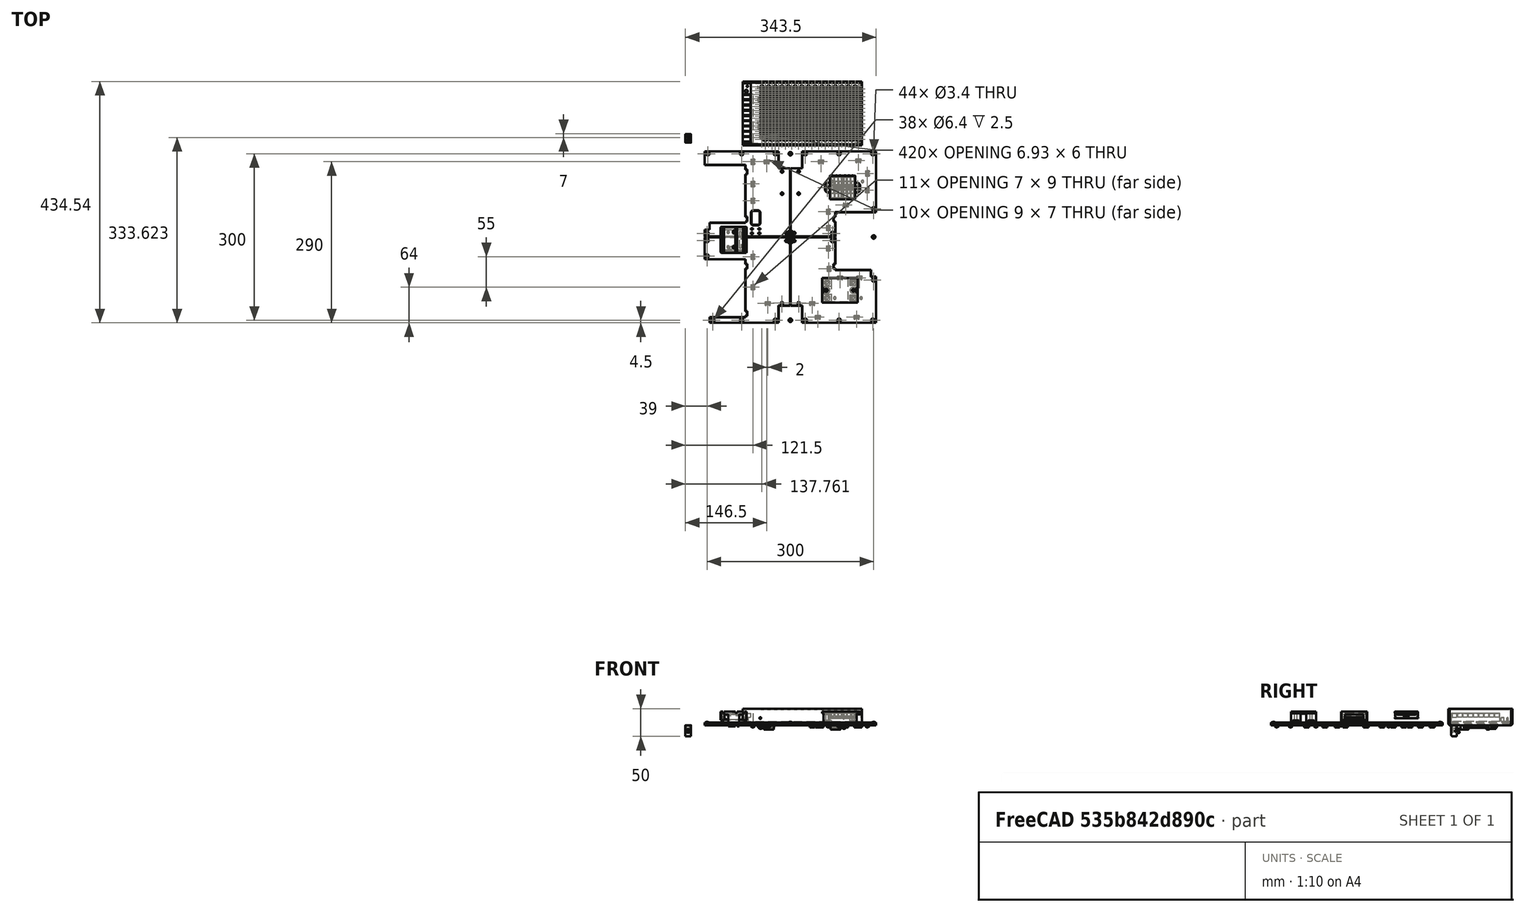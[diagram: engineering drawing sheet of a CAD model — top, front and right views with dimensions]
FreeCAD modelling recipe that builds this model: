
FCSTD DOCUMENT  (FreeCAD 0.19R24291 (Git))
Label: bottom-plate-180
License: All rights reserved
LicenseURL: http://en.wikipedia.org/wiki/All_rights_reserved
objects: Part::Feature×67, Part::MultiFuse×18, Part::Cylinder×16, Part::Box×9, Part::Cut×9, Part::FeaturePython×6, Part::Chamfer×5, App::Part×4, Part::MultiCommon×4
note: 134 computed .brp shape members not serialized (recipe doc carries the construction recipe); baked Part::Feature solids carry a one-line shape summary decoded from their .brp

FEATURE [Part::Feature] Cut001003002001  label="motor-cut-slot"
  Placement = pos=(-155,-155,0) rot=(0,0,1;0rad)
  shape: bbox 77 x 116.1 x 10 mm, 16 faces (baked)
FEATURE [Part::Box] Box  label="Cube"
  AttacherType = Attacher::AttachEngine3D
  Height = 5
  Length = 309
  Placement = pos=(-154.5,-154.5,0) rot=(0,0,1;0rad)
  Width = 309
FEATURE [Part::Feature] Cut001003002002  label="motor-cut-slot001"
  Placement = pos=(-155,15,0) rot=(0,0,1;0rad)
  shape: bbox 77 x 116.1 x 10 mm, 16 faces (baked)
FEATURE [Part::Feature] Part__Mirroring001  label="motor-cut-slot (Mirror #1)001"
  Placement = pos=(0,85,0) rot=(0,0,1;0rad)
  shape: bbox 77 x 116.1 x 10 mm, 16 faces (baked)
FEATURE [Part::MultiFuse] Fusion
  Shapes = -> [Part__Mirroring001,Cut001003002002,Cut001003002001]
FEATURE [Part::Cut] Cut
  Base = -> Box
  Tool = -> Fusion
FEATURE [Part::Box] Box002  label="Cube002"
  AttacherType = Attacher::AttachEngine3D
  Height = 10
  Length = 42
  Placement = pos=(-21,-155,0) rot=(0,0,1;0rad)
  Width = 31
FEATURE [Part::Box] Box003  label="Cube003"
  AttacherType = Attacher::AttachEngine3D
  Height = 10
  Length = 42
  Placement = pos=(-21,124,0) rot=(0,0,1;0rad)
  Width = 31
FEATURE [Part::MultiFuse] Fusion001
  Shapes = -> [Box003,Box002]
FEATURE [Part::Cut] Cut001003002003
  Base = -> Cut
  Tool = -> Fusion001
FEATURE [Part::Cylinder] Cylinder
  Angle = 360
  AttacherType = Attacher::AttachEngine3D
  Height = 10
  Placement = pos=(-15,-119,0) rot=(0,0,1;0rad)
  Radius = 1.7
FEATURE [Part::Cylinder] Cylinder001
  Angle = 360
  AttacherType = Attacher::AttachEngine3D
  Height = 10
  Placement = pos=(15,-119,0) rot=(0,0,1;0rad)
  Radius = 1.7
FEATURE [Part::Cylinder] Cylinder002
  Angle = 360
  AttacherType = Attacher::AttachEngine3D
  Height = 10
  Placement = pos=(-7,7,0) rot=(0,0,1;0rad)
  Radius = 1.9
FEATURE [Part::Cylinder] Cylinder003
  Angle = 360
  AttacherType = Attacher::AttachEngine3D
  Height = 10
  Placement = pos=(7,7,0) rot=(0,0,1;0rad)
  Radius = 1.9
FEATURE [Part::Cylinder] Cylinder004
  Angle = 360
  AttacherType = Attacher::AttachEngine3D
  Height = 10
  Placement = pos=(-7,-7,0) rot=(0,0,1;0rad)
  Radius = 1.9
FEATURE [Part::Cylinder] Cylinder005
  Angle = 360
  AttacherType = Attacher::AttachEngine3D
  Height = 10
  Placement = pos=(7,-7,0) rot=(0,0,1;0rad)
  Radius = 1.9
FEATURE [Part::MultiFuse] Fusion003
  Shapes = -> [Cylinder005,Cylinder002,Cylinder003,Cylinder004]
FEATURE [Part::Box] Box004  label="Cube004"
  AttacherType = Attacher::AttachEngine3D
  Height = 10
  Length = 310
  Placement = pos=(-155,-0.5,0) rot=(0,0,1;0rad)
  Width = 1
FEATURE [Part::Box] Box005  label="Cube005"
  AttacherType = Attacher::AttachEngine3D
  Height = 10
  Length = 1
  Placement = pos=(-0.5,-155,0) rot=(0,0,1;0rad)
  Width = 310
FEATURE [Part::MultiFuse] Fusion004  label="separatpr"
  Shapes = -> [Box005,Box004]
FEATURE [Part::Feature] Fusion005030001  label="bed-cable"
  Placement = pos=(35,-24,0) rot=(0,0,1;0rad)
  shape: bbox 15 x 42 x 10 mm, 34 faces, 5 solids (baked)
FEATURE [Part::Cylinder] Cylinder008
  Angle = 360
  AttacherType = Attacher::AttachEngine3D
  Height = 10
  Placement = pos=(-15,118,0) rot=(0,0,1;0rad)
  Radius = 1.9
FEATURE [Part::Cylinder] Cylinder009
  Angle = 360
  AttacherType = Attacher::AttachEngine3D
  Height = 10
  Placement = pos=(15,118,0) rot=(0,0,1;0rad)
  Radius = 1.9
FEATURE [Part::Cylinder] Cylinder010
  Angle = 360
  AttacherType = Attacher::AttachEngine3D
  Height = 10
  Placement = pos=(15,78,0) rot=(0,0,1;0rad)
  Radius = 1.9
FEATURE [Part::Cylinder] Cylinder011
  Angle = 360
  AttacherType = Attacher::AttachEngine3D
  Height = 10
  Placement = pos=(-15,78,0) rot=(0,0,1;0rad)
  Radius = 1.9
FEATURE [Part::MultiFuse] Fusion005030003
  Shapes = -> [Cylinder011,Cylinder008,Cylinder009,Cylinder010]
FEATURE [Part::Feature] Fusion005030004  label="bolt-slot"
  shape: bbox 6.4 x 6.4 x 6 mm, 7 faces (baked)
FEATURE [Part::Feature] Fusion005030005  label="bolt-slot_U"
  Placement = pos=(0,150,0) rot=(0,0,1;0rad)
  shape: bbox 6.4 x 6.4 x 6 mm, 7 faces (baked)
FEATURE [Part::Feature] Fusion005030006  label="bolt-slot_D"
  Placement = pos=(0,-150,0) rot=(0,0,1;0rad)
  shape: bbox 6.4 x 6.4 x 6 mm, 7 faces (baked)
FEATURE [Part::Feature] Fusion005030007  label="bolt-slot_L"
  Placement = pos=(-150,0,0) rot=(0,0,1;0rad)
  shape: bbox 6.4 x 6.4 x 6 mm, 7 faces (baked)
FEATURE [Part::Feature] Fusion005030008  label="bolt-slot_R"
  Placement = pos=(150,0,0) rot=(0,0,1;0rad)
  shape: bbox 6.4 x 6.4 x 6 mm, 7 faces (baked)
FEATURE [Part::Feature] Fusion005030009  label="bolt-slot_U001"
  Placement = pos=(-27,150,0) rot=(0,0,1;0rad)
  shape: bbox 6.4 x 6.4 x 6 mm, 7 faces (baked)
FEATURE [Part::Feature] Fusion005030010  label="bolt-slot_U002"
  Placement = pos=(27,150,0) rot=(0,0,1;0rad)
  shape: bbox 6.4 x 6.4 x 6 mm, 7 faces (baked)
FEATURE [Part::Feature] Fusion005030011  label="bolt-slot_U003"
  Placement = pos=(-148.5,150,0) rot=(0,0,1;0rad)
  shape: bbox 6.4 x 6.4 x 6 mm, 7 faces (baked)
FEATURE [Part::Feature] Fusion005030012  label="bolt-slot_U004"
  Placement = pos=(148.5,150,0) rot=(0,0,1;0rad)
  shape: bbox 6.4 x 6.4 x 6 mm, 7 faces (baked)
FEATURE [Part::Feature] Fusion005030013  label="bolt-slot_U005"
  Placement = pos=(-87.75,150,0) rot=(0,0,1;0rad)
  shape: bbox 6.4 x 6.4 x 6 mm, 7 faces (baked)
FEATURE [Part::Feature] Fusion005030014  label="bolt-slot_U006"
  Placement = pos=(87.75,150,0) rot=(0,0,1;0rad)
  shape: bbox 6.4 x 6.4 x 6 mm, 7 faces (baked)
FEATURE [Part::MultiFuse] Fusion005030015
  Shapes = -> [Fusion005030009,Fusion005030010,Fusion005030011,Fusion005030012,Fusion005030013,Fusion005030014]
FEATURE [Part::Feature] Fusion005030016  label="bolt-slot_D001"
  Placement = pos=(27,-150,0) rot=(0,0,1;0rad)
  shape: bbox 6.4 x 6.4 x 6 mm, 7 faces (baked)
FEATURE [Part::Feature] Fusion005030017  label="bolt-slot_D002"
  Placement = pos=(-27,-150,0) rot=(0,0,1;0rad)
  shape: bbox 6.4 x 6.4 x 6 mm, 7 faces (baked)
FEATURE [Part::Feature] Fusion005030018  label="bolt-slot_D003"
  Placement = pos=(148.5,-150,0) rot=(0,0,1;0rad)
  shape: bbox 6.4 x 6.4 x 6 mm, 7 faces (baked)
FEATURE [Part::Feature] Fusion005030019  label="bolt-slot_D004"
  Placement = pos=(-139.5,-150,0) rot=(0,0,1;0rad)
  shape: bbox 6.4 x 6.4 x 6 mm, 7 faces (baked)
FEATURE [Part::Feature] Fusion005030020  label="bolt-slot_D005"
  Placement = pos=(87.75,-150,0) rot=(0,0,1;0rad)
  shape: bbox 6.4 x 6.4 x 6 mm, 7 faces (baked)
FEATURE [Part::Feature] Fusion005030021  label="bolt-slot_D006"
  Placement = pos=(-87.75,-150,0) rot=(0,0,1;0rad)
  shape: bbox 6.4 x 6.4 x 6 mm, 7 faces (baked)
FEATURE [Part::MultiFuse] Fusion005030022
  Shapes = -> [Fusion005030021,Fusion005030016,Fusion005030017,Fusion005030018,Fusion005030019,Fusion005030020]
FEATURE [Part::Feature] Fusion005030023  label="bolt-slot_L001"
  Placement = pos=(-150,6.5,0) rot=(0,0,1;0rad)
  shape: bbox 6.4 x 6.4 x 6 mm, 7 faces (baked)
FEATURE [Part::Feature] Fusion005030024  label="bolt-slot_L002"
  Placement = pos=(-150,-6.5,0) rot=(0,0,1;0rad)
  shape: bbox 6.4 x 6.4 x 6 mm, 7 faces (baked)
FEATURE [Part::Feature] Fusion005030025  label="bolt-slot_L003"
  Placement = pos=(-150,-34.36,0) rot=(0,0,1;0rad)
  shape: bbox 6.4 x 6.4 x 6 mm, 7 faces (baked)
FEATURE [Part::MultiFuse] Fusion005030026
  Shapes = -> [Fusion005030025,Fusion005030023,Fusion005030024]
FEATURE [Part::Feature] Fusion005030027  label="bolt-slot_R001"
  Placement = pos=(150,50.64,0) rot=(0,0,1;0rad)
  shape: bbox 6.4 x 6.4 x 6 mm, 7 faces (baked)
FEATURE [Part::Feature] Fusion005030028  label="bolt-slot_R002"
  Placement = pos=(150,-77.5,0) rot=(0,0,1;0rad)
  shape: bbox 6.4 x 6.4 x 6 mm, 7 faces (baked)
FEATURE [Part::MultiFuse] Fusion005030029
  Shapes = -> [Fusion005030028,Fusion005030027]
FEATURE [Part::Cylinder] Cylinder012
  Angle = 360
  AttacherType = Attacher::AttachEngine3D
  Height = 4
  Placement = pos=(-112,8.5,0) rot=(0,0,1;0rad)
  Radius = 1.9
FEATURE [Part::Cylinder] Cylinder013
  Angle = 360
  AttacherType = Attacher::AttachEngine3D
  Height = 4
  Placement = pos=(-112,-18,0) rot=(0,0,1;0rad)
  Radius = 1.9
FEATURE [Part::MultiFuse] Fusion005030031
  Shapes = -> [Cylinder012,Cylinder013]
FEATURE [Part::Cylinder] Cylinder014
  Angle = 360
  AttacherType = Attacher::AttachEngine3D
  Height = 4
  Placement = pos=(75,100,0) rot=(0,0,1;0rad)
  Radius = 1.9
FEATURE [Part::Cylinder] Cylinder015
  Angle = 360
  AttacherType = Attacher::AttachEngine3D
  Height = 4
  Placement = pos=(130,100,0) rot=(0,0,1;0rad)
  Radius = 1.9
FEATURE [Part::Cylinder] Cylinder016
  Angle = 360
  AttacherType = Attacher::AttachEngine3D
  Height = 4
  Placement = pos=(80,-110,0) rot=(0,0,1;0rad)
  Radius = 1.9
FEATURE [Part::Cylinder] Cylinder017
  Angle = 360
  AttacherType = Attacher::AttachEngine3D
  Height = 4
  Placement = pos=(127.5,-110,0) rot=(0,0,1;0rad)
  Radius = 1.9
FEATURE [Part::Feature] Cut002001001  label="sonoff-mount"
  Placement = pos=(-102,-4.75,24.5) rot=(0.707107,-0.707107,0;3.14159rad)
  shape: bbox 47 x 47 x 26.5 mm, 108 faces (baked)
FEATURE [Part::Feature] Fusion006002011004053036004001028003005004  label="SonOff-mini"
  Placement = pos=(-102,-5,10) rot=(0.57735,-0.57735,0.57735;4.18879rad)
  shape: bbox 43.4 x 42.65 x 19.85 mm, 152 faces (baked)
FEATURE [Part::Feature] Cut009001  label="wago-mount"
  Placement = pos=(95,89,24.5) rot=(0.707107,0.707107,0;3.14159rad)
  shape: bbox 63.6 x 41.99 x 12.2 mm, 224 faces (baked)
FEATURE [Part::Feature] Part__Feature001  label="WAGO 222-3c-002"
  Placement = pos=(71.5,89.5,22.5) rot=(0.57735,-0.57735,0.57735;4.18879rad)
  shape: bbox 22.7 x 21.3 x 9.8 mm, 151 faces (baked)
FEATURE [Part::Feature] Part__Feature003  label="WAGO 222-3c-004"
  Placement = pos=(94.2,89.5,22.5) rot=(0.57735,0.57735,-0.57735;4.18879rad)
  shape: bbox 22.7 x 21.3 x 9.8 mm, 151 faces (baked)
FEATURE [Part::Feature] Part__Feature002  label="WAGO 222-3c-003"
  Placement = pos=(116.7,89.5,22.5) rot=(0.57735,0.57735,-0.57735;4.18879rad)
  shape: bbox 22.7 x 21.3 x 9.8 mm, 151 faces (baked)
FEATURE [Part::Feature] Part__Feature  label="WAGO 222-3c-001"
  Placement = pos=(94,89.5,22.5) rot=(0.57735,-0.57735,0.57735;4.18879rad)
  shape: bbox 22.7 x 21.3 x 9.8 mm, 151 faces (baked)
FEATURE [Part::Feature] Fusion006002011004053036004001028003005005  label="SSR0omron"
  Placement = pos=(89,-96,2.5) rot=(0.57735,-0.57735,0.57735;4.18879rad)
  shape: bbox 64 x 45 x 22.5 mm, 84 faces (baked)
FEATURE [App::Part] Part003  label="sonoff-switch"
  Group = -> [Fusion006002011004053036004001028003005004,Cut002001001]
  Origin = -> Origin003
  Placement = pos=(-10,0,-25) rot=(0,0,1;0rad)
FEATURE [App::Part] Part004  label="wago-connectors"
  Group = -> [Part__Feature001,Part__Feature003,Part__Feature002,Part__Feature,Cut009001]
  Origin = -> Origin004
  Placement = pos=(9,11,-25) rot=(0,0,1;0rad)
FEATURE [Part::FeaturePython] Washer001  label="M3-Washer"  # Fasteners workbench fastener (typed FeaturePython)
  Placement = pos=(113.418,-96,21.5) rot=(1,0,0;3.14159rad)
  baseObject = -> Fusion006002011004053036004001028003005005 [Edge76]
  diameter = 4
  invert = false
  matchOuter = true
  offset = 0
  type = 5
FEATURE [Part::FeaturePython] Washer  label="M3-Washer001"  # Fasteners workbench fastener (typed FeaturePython)
  Placement = pos=(65.4176,-96,21.5) rot=(1,0,0;3.14159rad)
  baseObject = -> Fusion006002011004053036004001028003005005 [Edge152]
  diameter = 4
  invert = false
  matchOuter = true
  offset = 0
  type = 5
FEATURE [App::Part] Part005  label="ssr"
  Group = -> [Washer001,Washer,Fusion006002011004053036004001028003005005]
  Origin = -> Origin005
  Placement = pos=(14,-14,-25) rot=(0,0,1;0rad)
FEATURE [Part::MultiFuse] Fusion006002011004053036004001028003005007
  Shapes = -> [Cylinder017,Cylinder016]
FEATURE [Part::MultiFuse] Fusion006002011004053036004001028003005008
  Shapes = -> [Cylinder015,Cylinder014]
FEATURE [Part::MultiFuse] Fusion006002011004053036004001028003005009
  Shapes = -> [Fusion006002011004053036004001028003005007,Fusion006002011004053036004001028003005008,Fusion005030031]
FEATURE [Part::Feature] Chamfer005007002017  label="ziptie015"
  Placement = pos=(135,80,3) rot=(0.707107,0.707107,0;3.14159rad)
  shape: bbox 7 x 9 x 7 mm, 14 faces (baked)
FEATURE [Part::Feature] Chamfer001001  label="ziptie"
  Placement = pos=(94,-77,3) rot=(0,1,0;3.14159rad)
  shape: bbox 9 x 7 x 7 mm, 14 faces (baked)
FEATURE [Part::Feature] Chamfer005007002003  label="ziptie001"
  Placement = pos=(124,-148,3) rot=(0,1,0;3.14159rad)
  shape: bbox 9 x 7 x 7 mm, 14 faces (baked)
FEATURE [Part::Feature] Chamfer005007002005  label="ziptie003"
  Placement = pos=(-71,-40,3) rot=(0.707107,0.707107,0;3.14159rad)
  shape: bbox 7 x 9 x 7 mm, 14 faces (baked)
FEATURE [Part::Feature] Chamfer005007002006  label="ziptie004"
  Placement = pos=(-71,91,3) rot=(0.707107,0.707107,0;3.14159rad)
  shape: bbox 7 x 9 x 7 mm, 14 faces (baked)
FEATURE [Part::Feature] Chamfer005007002008  label="ziptie006"
  Placement = pos=(65,-25,3) rot=(0.707107,0.707107,0;3.14159rad)
  shape: bbox 7 x 9 x 7 mm, 14 faces (baked)
FEATURE [Part::Feature] Chamfer005007002009  label="ziptie007"
  Placement = pos=(65,12,3) rot=(0.707107,0.707107,0;3.14159rad)
  shape: bbox 7 x 9 x 7 mm, 14 faces (baked)
FEATURE [Part::Feature] Chamfer005007002010  label="ziptie008"
  Placement = pos=(65,41,3) rot=(0.707107,0.707107,0;3.14159rad)
  shape: bbox 7 x 9 x 7 mm, 14 faces (baked)
FEATURE [Part::Feature] Chamfer005007002011  label="ziptie009"
  Placement = pos=(60,132,3) rot=(0,1,0;3.14159rad)
  shape: bbox 9 x 7 x 7 mm, 14 faces (baked)
FEATURE [Part::Feature] Chamfer005007002012  label="ziptie010"
  Placement = pos=(-38,132,3) rot=(0,1,0;3.14159rad)
  shape: bbox 9 x 7 x 7 mm, 14 faces (baked)
FEATURE [Part::Feature] Chamfer005007002013  label="ziptie011"
  Placement = pos=(66,-62,3) rot=(0.707107,0.707107,0;3.14159rad)
  shape: bbox 7 x 9 x 7 mm, 14 faces (baked)
FEATURE [Part::Feature] Chamfer005007002015  label="ziptie013"
  Placement = pos=(127,134,3) rot=(0,1,0;3.14159rad)
  shape: bbox 9 x 7 x 7 mm, 14 faces (baked)
FEATURE [Part::Feature] Fusion006002011004053036004001028003005014018035002002  label="lrs-psu"
  shape: bbox 215 x 115 x 30.01 mm, 2625 faces, 2 solids (baked)
FEATURE [Part::Feature] Part__Mirroring002  label="24v-200w-psu-mounter-mirror"
  Placement = pos=(-38.5,217.5,-2.7e-14) rot=(1,0,0;3.14159rad)
  shape: bbox 29 x 65.8 x 7.6 mm, 188 faces (baked)
FEATURE [Part::Feature] Fusion013001001  label="24v-200w-psu-mounter"
  Placement = pos=(81.5,217.5,-2.7e-14) rot=(1,0,0;3.14159rad)
  shape: bbox 29 x 65.8 x 7.6 mm, 188 faces (baked)
FEATURE [Part::FeaturePython] Screw052  label="M4x6-Screw012"  # Fasteners workbench fastener (typed FeaturePython)
  Placement = pos=(-53.5,247.5,-4) rot=(0,1,0;3.14159rad)
  baseObject = -> Part__Mirroring002 [Edge395]
  diameter = 2
  invert = false
  length = 0
  lengthCustom = 6
  matchOuter = true
  offset = 0
  thread = false
  type = 40
FEATURE [Part::FeaturePython] Screw053  label="M4x6-Screw013"  # Fasteners workbench fastener (typed FeaturePython)
  Placement = pos=(-53.5,197.5,-4) rot=(0,1,0;3.14159rad)
  baseObject = -> Part__Mirroring002 [Edge224]
  diameter = 2
  invert = false
  length = 0
  lengthCustom = 6
  matchOuter = true
  offset = 0
  thread = false
  type = 40
FEATURE [Part::FeaturePython] Screw054  label="M4x6-Screw"  # Fasteners workbench fastener (typed FeaturePython)
  Placement = pos=(96.5,247.5,-4) rot=(1,0,0;3.14159rad)
  baseObject = -> Fusion013001001 [Edge395]
  diameter = 2
  invert = true
  length = 0
  lengthCustom = 6
  matchOuter = true
  offset = 0
  thread = false
  type = 40
FEATURE [Part::FeaturePython] Screw055  label="M4x6-Screw014"  # Fasteners workbench fastener (typed FeaturePython)
  Placement = pos=(96.5,197.5,-4) rot=(1,0,0;3.14159rad)
  baseObject = -> Fusion013001001 [Edge224]
  diameter = 2
  invert = true
  length = 0
  lengthCustom = 6
  matchOuter = true
  offset = 0
  thread = false
  type = 40
FEATURE [App::Part] Part006  label="psu-24v"
  Group = -> [Fusion006002011004053036004001028003005014018035002002,Part__Mirroring002,Fusion013001001,Screw052,Screw053,Screw054,Screw055]
  Origin = -> Origin006
  Placement = pos=(222.6,21,-13) rot=(-0.707107,0.707107,0;3.14159rad)
FEATURE [Part::Feature] Chamfer005007002018  label="ziptie016"
  Placement = pos=(54,-148,3) rot=(0,1,0;3.14159rad)
  shape: bbox 9 x 7 x 7 mm, 14 faces (baked)
FEATURE [Part::Feature] Chamfer005007002019  label="ziptie017"
  Placement = pos=(-71,-95,3) rot=(0.707107,0.707107,0;3.14159rad)
  shape: bbox 7 x 9 x 7 mm, 14 faces (baked)
FEATURE [Part::Feature] Chamfer005007002020  label="ziptie018"
  Placement = pos=(-71,61,3) rot=(0.707107,0.707107,0;3.14159rad)
  shape: bbox 7 x 9 x 7 mm, 14 faces (baked)
FEATURE [Part::Feature] Chamfer005007002021  label="ziptie019"
  Placement = pos=(129,-77,3) rot=(0,1,0;3.14159rad)
  shape: bbox 9 x 7 x 7 mm, 14 faces (baked)
FEATURE [Part::Feature] Chamfer005007002022  label="ziptie020"
  Placement = pos=(135,110,3) rot=(0.707107,0.707107,0;3.14159rad)
  shape: bbox 7 x 9 x 7 mm, 14 faces (baked)
FEATURE [Part::Feature] Chamfer005007002023  label="ziptie021"
  Placement = pos=(95,61,3) rot=(1,0,0;3.14159rad)
  shape: bbox 9 x 7 x 7 mm, 14 faces (baked)
FEATURE [Part::Feature] Chamfer005007002024  label="ziptie022"
  Placement = pos=(-71,131,3) rot=(0.707107,0.707107,0;3.14159rad)
  shape: bbox 7 x 9 x 7 mm, 14 faces (baked)
FEATURE [Part::Feature] Chamfer005007002025  label="ziptie023"
  Placement = pos=(44,-123,3) rot=(0,1,0;3.14159rad)
  shape: bbox 9 x 7 x 7 mm, 14 faces (baked)
FEATURE [Part::Feature] Chamfer005007002026  label="ziptie024"
  Placement = pos=(-36,-123,3) rot=(0,1,0;3.14159rad)
  shape: bbox 9 x 7 x 7 mm, 14 faces (baked)
FEATURE [Part::MultiFuse] Fusion006002011004053036004001028003005014018035002003
  Shapes = -> [Chamfer005007002017,Chamfer001001,Chamfer005007002003,Chamfer005007002005,Chamfer005007002006,Chamfer005007002008,Chamfer005007002009,Chamfer005007002010,Chamfer005007002011,Chamfer005007002012,Chamfer005007002013,Chamfer005007002015,Chamfer005007002018,Chamfer005007002019,Chamfer005007002020,Chamfer005007002021,Chamfer005007002023,Chamfer005007002022,Chamfer005007002024,Chamfer005007002025,+1 more]
FEATURE [Part::Box] Box006  label="Cube006"
  AttacherType = Attacher::AttachEngine3D
  Height = 15
  Length = 155
  Placement = pos=(0,0,-9) rot=(0,0,1;0rad)
  Width = 155
FEATURE [Part::Box] Box007  label="Cube007"
  AttacherType = Attacher::AttachEngine3D
  Height = 15
  Length = 155
  Placement = pos=(-155,0,-9) rot=(0,0,1;0rad)
  Width = 155
FEATURE [Part::Box] Box008  label="Cube008"
  AttacherType = Attacher::AttachEngine3D
  Height = 15
  Length = 155
  Placement = pos=(0,-155,-9) rot=(0,0,1;0rad)
  Width = 155
FEATURE [Part::Box] Box009  label="Cube009"
  AttacherType = Attacher::AttachEngine3D
  Height = 15
  Length = 155
  Placement = pos=(-155,-155,-9) rot=(0,0,1;0rad)
  Width = 155
FEATURE [Part::Feature] Fusion006002011004053036004001028003005014018035002004  label="bolt-slot001"
  Placement = pos=(76,-6.5,0) rot=(0,0,1;0rad)
  shape: bbox 6.4 x 6.4 x 6 mm, 7 faces (baked)
FEATURE [Part::Feature] Fusion006002011004053036004001028003005014018035002005  label="bolt-slot002"
  Placement = pos=(76,6.5,0) rot=(0,0,1;0rad)
  shape: bbox 6.4 x 6.4 x 6 mm, 7 faces (baked)
FEATURE [Part::MultiFuse] Fusion006002011004053036004001028003005014018035002006
  Shapes = -> [Fusion006002011004053036004001028003005014018035002005,Fusion006002011004053036004001028003005014018035002004]
FEATURE [Part::MultiFuse] Fusion006002011004053036004001028003005014018035002007
  Shapes = -> [Fusion005030029,Fusion005030015,Fusion005030022,Fusion005030026,Fusion006002011004053036004001028003005014018035002006]
FEATURE [Part::Feature] Chamfer001  label="panel-side-connector"
  shape: bbox 10 x 23 x 5 mm, 32 faces (baked)
FEATURE [Part::Feature] Pocket003011  label="panel-mounter_U001"
  Placement = pos=(-179,180,-10) rot=(0.57735,-0.57735,-0.57735;2.0944rad)
  shape: bbox 10 x 15 x 20 mm, 54 faces (baked)
FEATURE [Part::MultiFuse] Fusion006002011004053036004001028003005014018035002008
  Shapes = -> [Cylinder001,Cylinder]
FEATURE [Part::Cut] Cut001003002004
  Base = -> Cut001003002003
  Tool = -> Fusion006002011004053036004001028003005014018035002008
FEATURE [Part::Cut] Cut001003002005
  Base = -> Cut001003002004
  Tool = -> Fusion006002011004053036004001028003005014018035002007
FEATURE [Part::Cut] Cut001003002006
  Base = -> Cut001003002005
  Tool = -> Fusion005030001
FEATURE [Part::Cut] Cut001003002007
  Base = -> Cut001003002006
  Tool = -> Fusion006002011004053036004001028003005009
FEATURE [Part::Cut] Cut001003002008
  Base = -> Cut001003002007
  Tool = -> Fusion005030003
FEATURE [Part::Cut] Cut001003002009
  Base = -> Cut001003002008
  Tool = -> Fusion003
FEATURE [Part::MultiFuse] Fusion006002011004053036004001028003005014018035002009
  Shapes = -> [Fusion006002011004053036004001028003005014018035002003,Cut001003002009]
FEATURE [Part::Cut] Cut001003002010  label="panel-combined"
  Base = -> Fusion006002011004053036004001028003005014018035002009
  Tool = -> Fusion004
FEATURE [Part::Feature] Cut001003002010001  label="panel-combined001"
  shape: bbox 309 x 309 x 9 mm, 490 faces, 4 solids (baked)
FEATURE [Part::Feature] Cut001003002010002  label="panel-combined002"
  shape: bbox 309 x 309 x 9 mm, 490 faces, 4 solids (baked)
FEATURE [Part::Feature] Cut001003002010003  label="panel-combined003"
  shape: bbox 309 x 309 x 9 mm, 490 faces, 4 solids (baked)
FEATURE [Part::Feature] Cut001003002010004  label="panel-combined004"
  shape: bbox 309 x 309 x 9 mm, 490 faces, 4 solids (baked)
FEATURE [Part::MultiCommon] Common
  Shapes = -> [Box009,Cut001003002010001]
FEATURE [Part::MultiCommon] Common001
  Shapes = -> [Cut001003002010002,Box008]
FEATURE [Part::MultiCommon] Common002
  Shapes = -> [Cut001003002010003,Box007]
FEATURE [Part::MultiCommon] Common003
  Shapes = -> [Cut001003002010004,Box006]
FEATURE [Part::Chamfer] Chamfer
  Base = -> Common003
  Edges = 32 edges r=0.4: [Edge44,Edge45,Edge46,Edge47,Edge48,Edge49,Edge50,Edge51,Edge52,Edge53,Edge54,Edge55,Edge56,Edge83,Edge84,Edge85,Edge96,Edge115,Edge119,Edge120,Edge123,Edge124,Edge127,Edge128,Edge131,Edge133,Edge134,Edge136,Edge138,Edge139,Edge205,Edge209]
FEATURE [Part::Chamfer] Chamfer005007002027
  Base = -> Common
  Edges = 41 edges r=0.4: [Edge1,Edge2,Edge3,Edge4,Edge5,Edge6,Edge7,Edge8,Edge9,Edge10,Edge11,Edge12,Edge13,Edge14,Edge15,Edge16,Edge17,Edge18,Edge22,Edge25,Edge27,Edge29,Edge31,Edge34,Edge36,Edge37,Edge40,Edge41,Edge44,Edge46,Edge48,Edge50,Edge52,Edge54,Edge56,Edge58,Edge60,Edge61,Edge69,Edge75,Edge97]
FEATURE [Part::Chamfer] Chamfer005007002028
  Base = -> Common001
  Edges = 34 edges r=0.4: [Edge1,Edge2,Edge3,Edge4,Edge5,Edge6,Edge7,Edge8,Edge9,Edge10,Edge11,Edge12,Edge13,Edge14,Edge16,Edge43,Edge44,Edge54,Edge81,Edge83,Edge86,Edge88,Edge89,Edge91,Edge93,Edge96,Edge97,Edge99,Edge101,Edge103,Edge105,Edge107,Edge110,Edge202]
FEATURE [Part::Chamfer] Chamfer005007002029
  Base = -> Common002
  Edges = 47 edges r=0.4: [Edge1,Edge2,Edge3,Edge4,Edge5,Edge6,Edge7,Edge8,Edge9,Edge10,Edge11,Edge12,Edge13,Edge14,Edge15,Edge16,Edge17,Edge18,Edge19,Edge20,Edge22,Edge47,Edge66,Edge83,Edge85,Edge89,Edge90,Edge93,Edge94,Edge97,Edge98,Edge100,Edge102,Edge105,Edge106,Edge108,Edge110,Edge112,Edge114,Edge117,Edge119,Edge121,+5 more]
FEATURE [Part::Chamfer] Chamfer005007002030
  Base = -> Chamfer005007002029
  Edges = 32 edges r=1: [Edge22,Edge24,Edge26,Edge28,Edge30,Edge32,Edge34,Edge36,Edge38,Edge39,Edge40,Edge41,Edge42,Edge43,Edge44,Edge45,Edge128,Edge134,Edge136,Edge142,Edge144,Edge150,Edge152,Edge158,Edge160,Edge162,Edge165,Edge166,Edge169,Edge171,Edge172,Edge174]
FEATURE [Part::Feature] Chamfer005007002030001
  shape: bbox 154 x 154 x 9 mm, 202 faces (baked)
